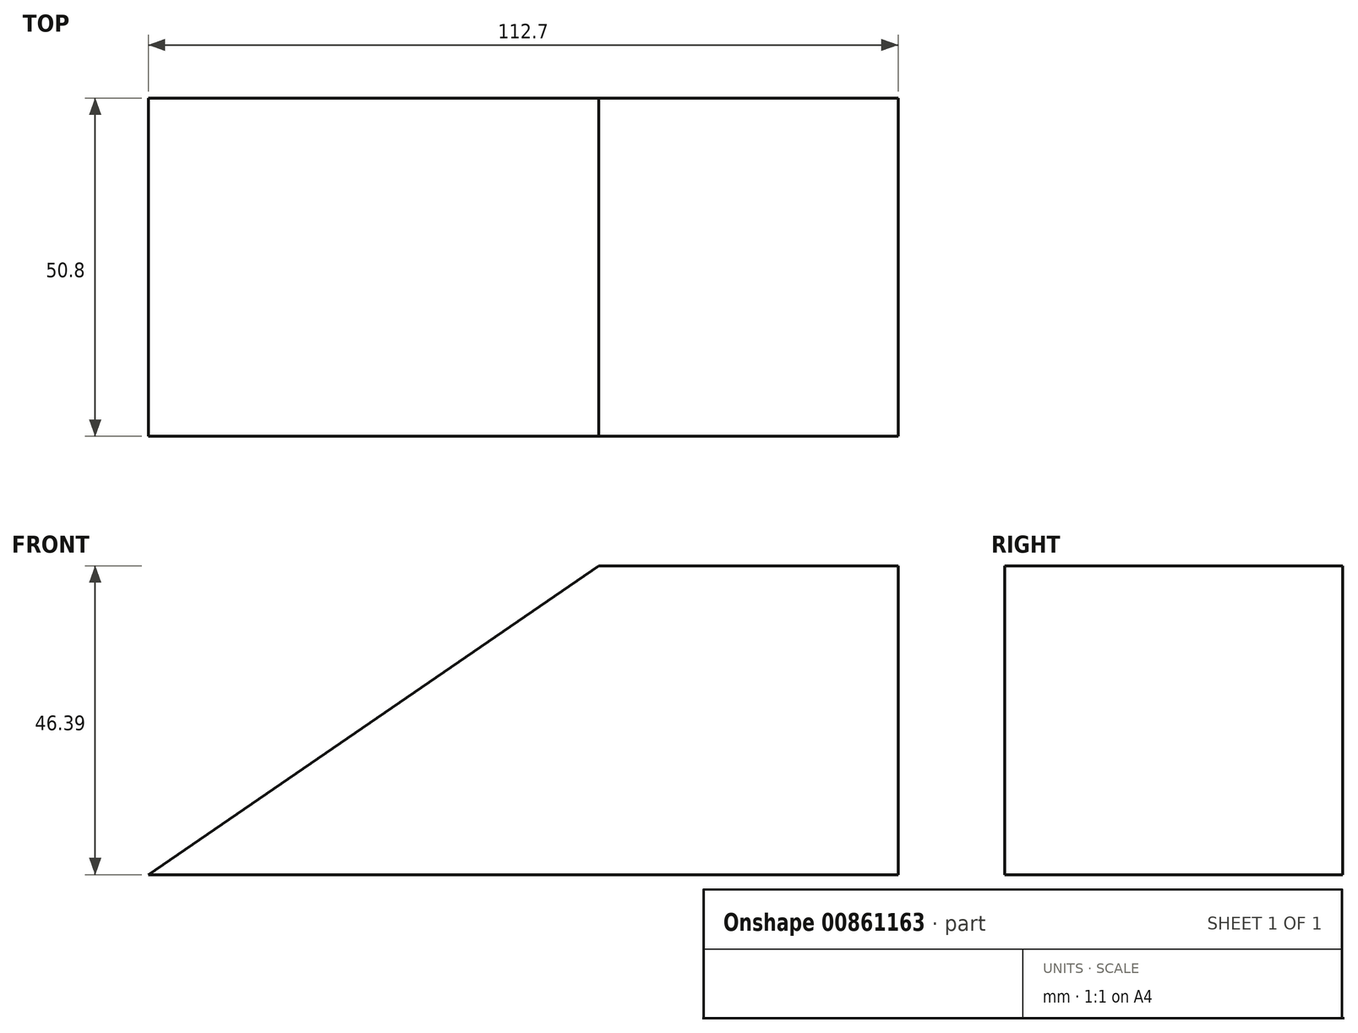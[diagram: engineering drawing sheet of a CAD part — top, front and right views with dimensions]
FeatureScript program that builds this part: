
annotation { "Feature Type Name" : "Feature", "Feature Type Description" : "" }
export const myFeature = defineFeature(function(context is Context, id is Id, definition is map)
    precondition{}
    {
        {
            var Q0;
            Q0=qCreatedBy(makeId("Front.planeOp"),FACE);
            var sketch = newSketch(context, id + "F0", { "sketchPlane" : qUnion([Q0])});
            skLineSegment(sketch, "E0", {"start": v(0, 0) * mm, "end": v(67.69, 46.4) * mm});
            skLineSegment(sketch, "E1", {"start": v(67.69, 46.4) * mm, "end": v(112.7, 46.4) * mm});
            skLineSegment(sketch, "E2", {"start": v(112.7, 46.4) * mm, "end": v(112.7, 0) * mm});
            skLineSegment(sketch, "E3", {"start": v(112.7, 0) * mm, "end": v(0, 0) * mm});
            skSolve(sketch);
        }
        {
            var Q0;
            Q0 = qSketchRegion(id + "F0", true);
            extrude(context, id + "F1", {"entities" : qUnion([Q0]), "depth" : 50.8 * mm, "offsetDistance" : 25.4 * mm});
        }
    });
